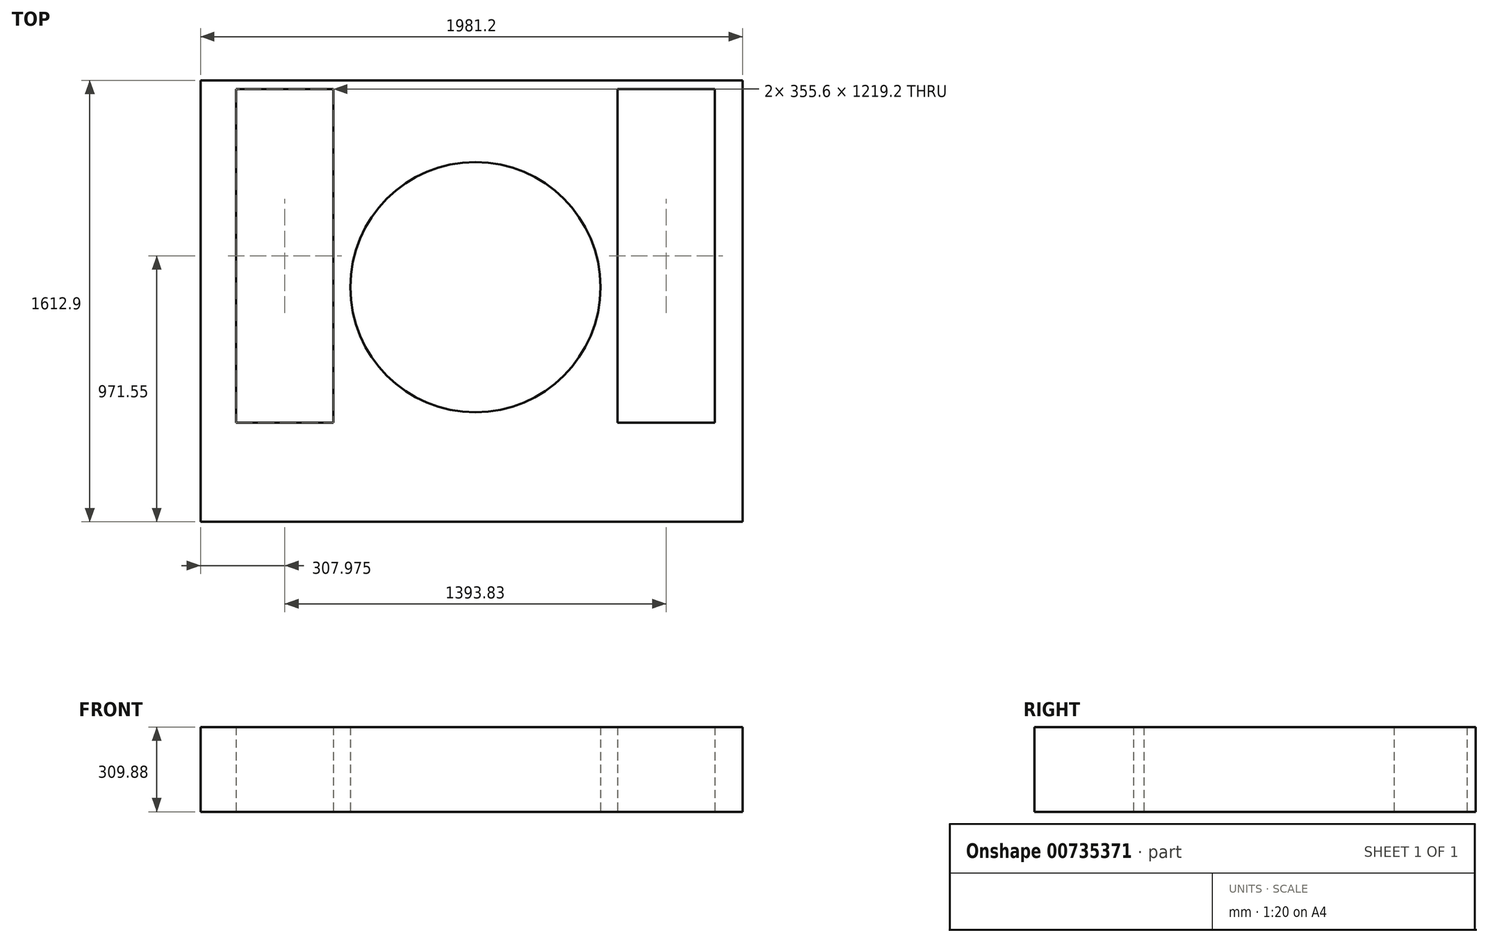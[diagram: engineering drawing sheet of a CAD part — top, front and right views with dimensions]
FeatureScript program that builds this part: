
annotation { "Feature Type Name" : "Feature", "Feature Type Description" : "" }
export const myFeature = defineFeature(function(context is Context, id is Id, definition is map)
    precondition{}
    {
        {
            var Q0;
            Q0=qCreatedBy(makeId("Top.planeOp"),FACE);
            var sketch = newSketch(context, id + "F0", { "sketchPlane" : qUnion([Q0])});
            skLineSegment(sketch, "E0.bottom", {"start": v(-1219.2, 857.25) * mm, "end": v(1219.2, 857.25) * mm});
            skLineSegment(sketch, "E0.top", {"start": v(-1219.2, -857.25) * mm, "end": v(1219.2, -857.25) * mm});
            skLineSegment(sketch, "E0.left", {"start": v(-1219.2, 857.25) * mm, "end": v(-1219.2, -857.25) * mm});
            skLineSegment(sketch, "E0.right", {"start": v(1219.2, 857.25) * mm, "end": v(1219.2, -857.25) * mm});
            skPoint(sketch, "E0.middle", {"position": v(0, 0) * mm});
            skLineSegment(sketch, "E1", {"start": v(-1219.2, 755.65) * mm, "end": v(762, 755.65) * mm});
            skLineSegment(sketch, "E2", {"start": v(762, 755.65) * mm, "end": v(762, -857.25) * mm});
            skLineSegment(sketch, "E3.bottom", {"start": v(-1089.03, 723.9) * mm, "end": v(-733.43, 723.9) * mm});
            skLineSegment(sketch, "E3.top", {"start": v(-1089.03, -495.3) * mm, "end": v(-733.43, -495.3) * mm});
            skLineSegment(sketch, "E3.left", {"start": v(-1089.03, 723.9) * mm, "end": v(-1089.03, -495.3) * mm});
            skLineSegment(sketch, "E3.right", {"start": v(-733.43, 723.9) * mm, "end": v(-733.43, -495.3) * mm});
            skLineSegment(sketch, "E4.bottom", {"start": v(304.8, 723.9) * mm, "end": v(660.4, 723.9) * mm});
            skLineSegment(sketch, "E4.top", {"start": v(304.8, -495.3) * mm, "end": v(660.4, -495.3) * mm});
            skLineSegment(sketch, "E4.left", {"start": v(304.8, 723.9) * mm, "end": v(304.8, -495.3) * mm});
            skLineSegment(sketch, "E4.right", {"start": v(660.4, 723.9) * mm, "end": v(660.4, -495.3) * mm});
            skCircle(sketch, "E5", {"center": v(-214.31, 0) * mm, "radius": 457.2 * mm});
            skSolve(sketch);
        }
        {
            var Q0;
            {var subQ4=sQuery(id+"F0.wireOp",EDGE,"E1");Q0=makeQuery(id+"F0.imprint","IMPRINT",FACE,{"disambiguationData":[TD([[makeQuery(id+"F0.imprint","IMPRINT",EDGE,{"derivedFrom":subQ4}),-1.0]])]});}
            extrude(context, id + "F1", {"entities" : qUnion([Q0]), "depth" : 101.6 * mm, "offsetDistance" : 25.4 * mm});
        }
        {
            var Q0;
            Q0=makeQuery(id+"F1.opExtrude","CAP_FACE",FACE,{"disambiguationData":[OSD([sQuery(id+"F0.wireOp",EDGE,"E0.top"),sQuery(id+"F0.wireOp",EDGE,"E0.left"),sQuery(id+"F0.wireOp",EDGE,"E1"),sQuery(id+"F0.wireOp",EDGE,"E2"),sQuery(id+"F0.wireOp",EDGE,"E3.bottom"),sQuery(id+"F0.wireOp",EDGE,"E3.top"),sQuery(id+"F0.wireOp",EDGE,"E3.left"),sQuery(id+"F0.wireOp",EDGE,"E3.right"),sQuery(id+"F0.wireOp",EDGE,"E4.bottom"),sQuery(id+"F0.wireOp",EDGE,"E4.top"),sQuery(id+"F0.wireOp",EDGE,"E4.left"),sQuery(id+"F0.wireOp",EDGE,"E4.right"),sQuery(id+"F0.wireOp",EDGE,"E5")])],"isStart":false});
            extrude(context, id + "F2", {"entities" : qUnion([Q0]), "operationType" : NewBodyOperationType.ADD, "depth" : 208.28 * mm, "offsetDistance" : 25.4 * mm});
        }
        {
            var Q0;
            Q0=makeQuery(id+"F2.opExtrude","CAP_FACE",FACE,{"disambiguationData":[OSD([sQuery(id+"F0.wireOp",EDGE,"E0.top"),sQuery(id+"F0.wireOp",EDGE,"E0.left"),sQuery(id+"F0.wireOp",EDGE,"E1"),sQuery(id+"F0.wireOp",EDGE,"E2"),sQuery(id+"F0.wireOp",EDGE,"E3.bottom"),sQuery(id+"F0.wireOp",EDGE,"E3.top"),sQuery(id+"F0.wireOp",EDGE,"E3.left"),sQuery(id+"F0.wireOp",EDGE,"E3.right"),sQuery(id+"F0.wireOp",EDGE,"E4.bottom"),sQuery(id+"F0.wireOp",EDGE,"E4.top"),sQuery(id+"F0.wireOp",EDGE,"E4.left"),sQuery(id+"F0.wireOp",EDGE,"E4.right"),sQuery(id+"F0.wireOp",EDGE,"E5")])],"isStart":false});
            var sketch = newSketch(context, id + "F3", { "sketchPlane" : qUnion([Q0])});
            skSolve(sketch);
        }
        {
            var Q0;
            Q0=makeQuery(id+"F3.imprint","IMPRINT",FACE,{"disambiguationData":[TD([[makeQuery(id+"F3.imprint","IMPRINT",EDGE,{"derivedFrom":makeQuery(id+"F2.opExtrude","CAP_EDGE",EDGE,{"disambiguationData":[OSD([sQuery(id+"F0.wireOp",EDGE,"E0.top")])],"isStart":false})}),1.0]])]});
            var sketch = newSketch(context, id + "F4", { "sketchPlane" : qUnion([Q0])});
            skCircle(sketch, "E6", {"center": v(-535.13, -657.43) * mm, "radius": 130.53 * mm});
            skSolve(sketch);
        }
        {
            var Q0;
            Q0=sQuery(id+"F4.wireOp",EDGE,"E6");
            extrude(context, id + "F5", {"bodyType" : ToolBodyType.SURFACE, "surfaceEntities" : qUnion([Q0]), "depth" : -152.4 * mm, "offsetDistance" : 25.4 * mm});
        }
    });
